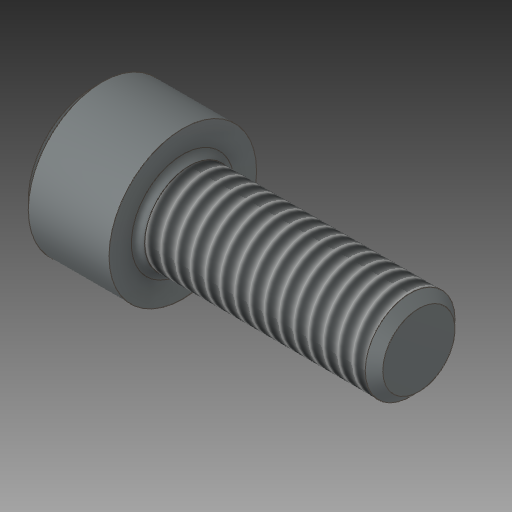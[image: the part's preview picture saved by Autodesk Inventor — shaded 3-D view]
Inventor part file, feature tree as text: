
AUTODESK INVENTOR PART (.ipt)
format: ipt  version: 2017.1 (Build 211199000, 199)  size: 196,096 bytes
history: native  units: in
note: dims shown in document units (in); Inventor stores cm internally (conversion verified against a paired STEP export)
features: thread x1, other x1
ambient origin geometry x8: Origin, YZ Plane, XZ Plane, XY Plane, X Axis, Y Axis, Z Axis, Center Point
bodies: Solid1 (feature_tree)
feature tree (2):
  thread  "Thread1"  [1 undecoded]
  other  "Hex"
note: 1 required parameter value undecoded (feature->parameter linkage not recoverable at this tier; creation-order binding heuristic only, values carry confidence <= 0.55)
